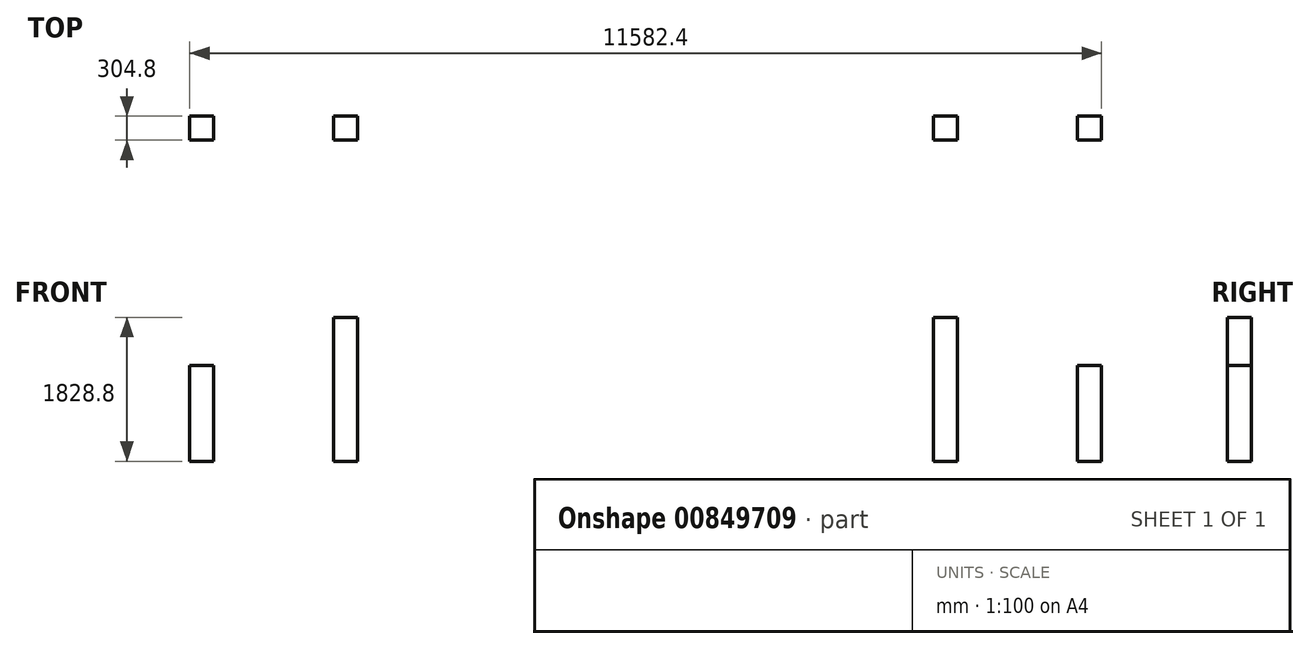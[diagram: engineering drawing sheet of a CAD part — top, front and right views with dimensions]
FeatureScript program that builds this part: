
annotation { "Feature Type Name" : "Feature", "Feature Type Description" : "" }
export const myFeature = defineFeature(function(context is Context, id is Id, definition is map)
    precondition{}
    {
        {
            var Q0;
            Q0=qCreatedBy(makeId("Top.planeOp"),FACE);
            var sketch = newSketch(context, id + "F0", { "sketchPlane" : qUnion([Q0])});
            skLineSegment(sketch, "E0", {"start": v(0, 0) * mm, "end": v(-3657.6, 0) * mm, "construction": true});
            skLineSegment(sketch, "E1", {"start": v(0, 0) * mm, "end": v(3657.6, 0) * mm, "construction": true});
            skPoint(sketch, "E2.MirrorCS.end.orphan", {"position": v(-3962.4, 0) * mm});
            skPoint(sketch, "E2.MirrorCS.start.orphan", {"position": v(-3657.6, 0) * mm});
            skLineSegment(sketch, "E3", {"start": v(0, 0) * mm, "end": v(0, -437.71) * mm, "construction": true});
            skLineSegment(sketch, "E4", {"start": v(-3657.6, 0) * mm, "end": v(-3657.6, 152.4) * mm});
            skLineSegment(sketch, "E5", {"start": v(-3657.6, 152.4) * mm, "end": v(-3962.4, 152.4) * mm});
            skLineSegment(sketch, "E6", {"start": v(-3962.4, 152.4) * mm, "end": v(-3962.4, -152.4) * mm});
            skLineSegment(sketch, "E7", {"start": v(-3962.4, -152.4) * mm, "end": v(-3657.6, -152.4) * mm});
            skLineSegment(sketch, "E8", {"start": v(-3657.6, -152.4) * mm, "end": v(-3657.6, 0) * mm});
            skLineSegment(sketch, "E9.MirrorCS", {"start": v(3657.6, 0) * mm, "end": v(3657.6, 152.4) * mm});
            skLineSegment(sketch, "E10.MirrorCS", {"start": v(3657.6, 152.4) * mm, "end": v(3962.4, 152.4) * mm});
            skLineSegment(sketch, "E11.MirrorCS", {"start": v(3962.4, 152.4) * mm, "end": v(3962.4, -152.4) * mm});
            skLineSegment(sketch, "E12.MirrorCS", {"start": v(3962.4, -152.4) * mm, "end": v(3657.6, -152.4) * mm});
            skLineSegment(sketch, "E13.MirrorCS", {"start": v(3657.6, -152.4) * mm, "end": v(3657.6, 0) * mm});
            skLineSegment(sketch, "E14", {"start": v(-3657.6, 0) * mm, "end": v(-6096, 0) * mm, "construction": true});
            skLineSegment(sketch, "E15.MirrorCS", {"start": v(3657.6, 0) * mm, "end": v(6096, 0) * mm, "construction": true});
            skSolve(sketch);
        }
        {
            var Q0;
            Q0 = qSketchRegion(id + "F0", true);
            extrude(context, id + "F1", {"entities" : qUnion([Q0]), "depth" : 1828.8 * mm, "offsetDistance" : 25.4 * mm});
        }
        {
            var Q0;
            Q0=qCreatedBy(makeId("Top.planeOp"),FACE);
            var sketch = newSketch(context, id + "F2", { "sketchPlane" : qUnion([Q0])});
            skLineSegment(sketch, "E16", {"start": v(0, 0) * mm, "end": v(-5486.4, 0) * mm, "construction": true});
            skLineSegment(sketch, "E17", {"start": v(0, 0) * mm, "end": v(5486.4, 0) * mm, "construction": true});
            skLineSegment(sketch, "E18", {"start": v(-5486.4, 0) * mm, "end": v(-5486.4, 152.4) * mm});
            skLineSegment(sketch, "E19", {"start": v(-5486.4, 152.4) * mm, "end": v(-5791.2, 152.4) * mm});
            skLineSegment(sketch, "E20", {"start": v(-5791.2, 152.4) * mm, "end": v(-5791.2, -152.4) * mm});
            skLineSegment(sketch, "E21", {"start": v(-5791.2, -152.4) * mm, "end": v(-5486.4, -152.4) * mm});
            skLineSegment(sketch, "E22", {"start": v(-5486.4, -152.4) * mm, "end": v(-5486.4, 0) * mm});
            skLineSegment(sketch, "E23.MirrorCS", {"start": v(5486.4, 0) * mm, "end": v(5486.4, 152.4) * mm});
            skLineSegment(sketch, "E24.MirrorCS", {"start": v(5486.4, -152.4) * mm, "end": v(5486.4, 0) * mm});
            skLineSegment(sketch, "E25.MirrorCS", {"start": v(5791.2, -152.4) * mm, "end": v(5486.4, -152.4) * mm});
            skLineSegment(sketch, "E26.MirrorCS", {"start": v(5486.4, 152.4) * mm, "end": v(5791.2, 152.4) * mm});
            skLineSegment(sketch, "E27.MirrorCS", {"start": v(5791.2, 152.4) * mm, "end": v(5791.2, -152.4) * mm});
            skSolve(sketch);
        }
        {
            var Q0;
            Q0 = qSketchRegion(id + "F2", true);
            extrude(context, id + "F3", {"entities" : qUnion([Q0]), "depth" : 1219.2 * mm, "offsetDistance" : 25.4 * mm});
        }
    });
